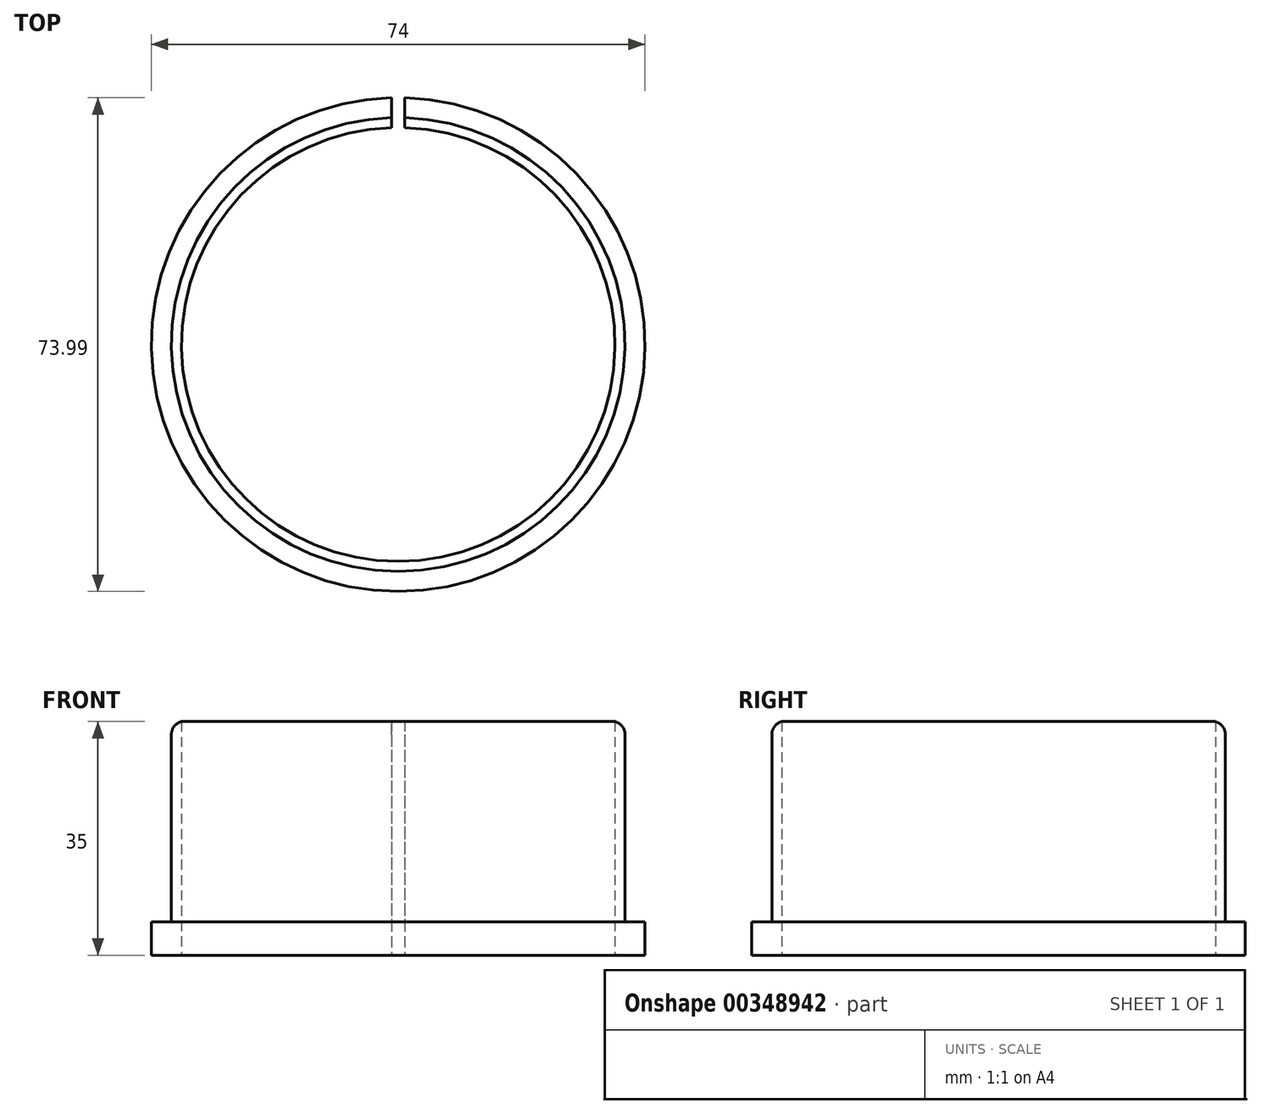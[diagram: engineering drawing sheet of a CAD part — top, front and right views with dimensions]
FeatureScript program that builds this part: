
annotation { "Feature Type Name" : "Feature", "Feature Type Description" : "" }
export const myFeature = defineFeature(function(context is Context, id is Id, definition is map)
    precondition{}
    {
        {
            var Q0;
            Q0=qCreatedBy(makeId("Top.planeOp"),FACE);
            var sketch = newSketch(context, id + "F0", { "sketchPlane" : qUnion([Q0]), "disableImprinting" : false});
            skCircle(sketch, "E0", {"center": v(0, 0) * mm, "radius": 32.5 * mm});
            skCircle(sketch, "E1", {"center": v(0, 0) * mm, "radius": 34 * mm});
            skCircle(sketch, "E2", {"center": v(0, 0) * mm, "radius": 37 * mm});
            skLineSegment(sketch, "E3.bottom", {"start": v(1, -11.18) * mm, "end": v(-1, -11.18) * mm});
            skLineSegment(sketch, "E3.top", {"start": v(1, 78.82) * mm, "end": v(-1, 78.82) * mm});
            skLineSegment(sketch, "E3.left", {"start": v(1, -11.18) * mm, "end": v(1, 78.82) * mm});
            skLineSegment(sketch, "E3.right", {"start": v(-1, -11.18) * mm, "end": v(-1, 78.82) * mm});
            skPoint(sketch, "E3.middle", {"position": v(0, 33.82) * mm});
            skSolve(sketch);
        }
        {
            var Q0;
            Q0=makeQuery(id+"F0.imprint","IMPRINT",FACE,{"disambiguationData":[TD([[makeQuery(id+"F0.imprint","IMPRINT",EDGE,{"derivedFrom":sQuery(id+"F0.wireOp",EDGE,"E0")}),-1.0]])]});
            extrude(context, id + "F1", {"entities" : qUnion([Q0]), "flatOperationType" : FlatOperationType.REMOVE, "offsetDistance" : 25 * mm, "depth" : 35 * mm, "domain" : OperationDomain.MODEL});
        }
        {
            var Q0;
            Q0=makeQuery(id+"F0.imprint","IMPRINT",FACE,{"disambiguationData":[TD([[makeQuery(id+"F0.imprint","IMPRINT",EDGE,{"derivedFrom":sQuery(id+"F0.wireOp",EDGE,"E1")}),-1.0]])]});
            extrude(context, id + "F2", {"entities" : qUnion([Q0]), "operationType" : NewBodyOperationType.ADD, "depth" : 5 * mm});
        }
        {
            var Q0;
            {var subQ5=sQuery(id+"F0.wireOp",EDGE,"E3.top");Q0=makeQuery(id+"F0.imprint","IMPRINT",FACE,{"disambiguationData":[TD([[makeQuery(id+"F0.imprint","IMPRINT",EDGE,{"derivedFrom":subQ5}),1.0]])]});}
            var Q1;
            {var subQ0=sQuery(id+"F0.wireOp",EDGE,"E3.left");var subQ1=sQuery(id+"F0.wireOp",EDGE,"E1");var subQ2=makeQuery(id+"F0.imprint","INTERSECT",VERTEX,{"derivedFrom":[subQ1,subQ0]});Q1=makeQuery(id+"F0.imprint","IMPRINT",FACE,{"disambiguationData":[TD([[makeQuery(id+"F0.imprint","IMPRINT",EDGE,{"disambiguationData":[TD([[subQ2,-1.0]])],"derivedFrom":subQ1}),-1.0]])]});}
            var Q2;
            {var subQ0=sQuery(id+"F0.wireOp",EDGE,"E3.left");var subQ1=sQuery(id+"F0.wireOp",EDGE,"E0");var subQ2=makeQuery(id+"F0.imprint","INTERSECT",VERTEX,{"derivedFrom":[subQ1,subQ0]});Q2=makeQuery(id+"F0.imprint","IMPRINT",FACE,{"disambiguationData":[TD([[makeQuery(id+"F0.imprint","IMPRINT",EDGE,{"disambiguationData":[TD([[subQ2,-1.0]])],"derivedFrom":subQ1}),-1.0]])]});}
            var Q3;
            {var subQ5=sQuery(id+"F0.wireOp",EDGE,"E3.bottom");Q3=makeQuery(id+"F0.imprint","IMPRINT",FACE,{"disambiguationData":[TD([[makeQuery(id+"F0.imprint","IMPRINT",EDGE,{"derivedFrom":subQ5}),-1.0]])]});}
            extrude(context, id + "F3", {"entities" : qUnion([Q0, Q1, Q2, Q3]), "operationType" : NewBodyOperationType.REMOVE, "endBound" : BoundingType.THROUGH_ALL, "depth" : 30 * mm});
        }
        {
            var Q0;
            Q0=makeQuery(id+"F1.opExtrude","CAP_EDGE",EDGE,{"disambiguationData":[OSD([sQuery(id+"F0.wireOp",EDGE,"E1")])],"isStart":false});
            fillet(context, id + "F4", {"entities" : qUnion([Q0]), "radius" : 2 * mm, "tangentPropagation" : true, "allowEdgeOverflow" : false});
        }
    });
